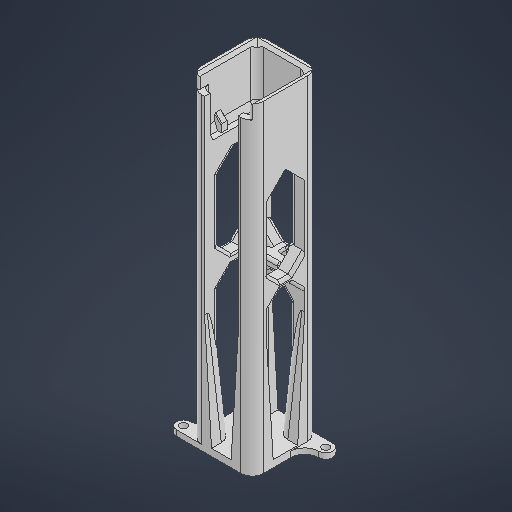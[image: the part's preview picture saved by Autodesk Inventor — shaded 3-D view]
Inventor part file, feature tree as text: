
AUTODESK INVENTOR PART (.ipt)
format: ipt  version: 2025.1 (Build 291241000, 241)  size: 1,649,152 bytes
history: native  units: mm
features: chamfer x13, extrude x10, fillet x10, sketch x7, plane x1, projected_geometry x1
ambient origin geometry x8: Origin, YZ Plane, XZ Plane, XY Plane, X Axis, Y Axis, Z Axis, Center Point
bodies: Solid1 (feature_tree)
feature tree (42):
  sketch  "Sketch1"  dims[d0=39.5mm d1=36.0mm]
  extrude  "Extrusion1"  Depth=36.0mm
  extrude  "Extrusion2"  Depth=47.5mm
  extrude  "Extrusion3"  Depth=6.0mm
  sketch  "Sketch2"  dims[d2=4.0mm d3=47.5mm]
  extrude  "Extrusion4"  Depth=5.0mm
  extrude  "Extrusion5"  Depth=10.0mm TaperAngle=0.0deg
  chamfer  "Chamfer1"  Distance=30.0mm
  chamfer  "Chamfer2"  Distance=180.0mm
  chamfer  "Chamfer4"  Distance=5.0mm
  plane  "Work Plane1"
  chamfer  "Chamfer5"  Distance=5.0mm Angle=45.0deg
  extrude  "Extrusion6"  Depth=4.8mm TaperAngle=45.0deg
  chamfer  "Chamfer6"  Distance=2.0mm Angle=45.0deg
  extrude  "Extrusion7"  Depth=4.8mm TaperAngle=45.0deg
  fillet  "Fillet1"  Radius=70.0mm
  fillet  "Fillet2"  Radius=5.0mm
  fillet  "Fillet3"  Radius=10.0mm
  fillet  "Fillet4"  Radius=10.0mm
  fillet  "Fillet5"  Radius=10.0mm
  extrude  "Extrusion8"  Depth=4.8mm
  sketch  "Sketch6"  dims[d8=10.0mm d9=0.0mm d10=40.0mm d11=0.0mm d12=30.0mm d13=0.0mm]
  extrude  "Extrusion9"  Depth=4.8mm
  chamfer  "Chamfer10"  Distance=10.0mm
  chamfer  "Chamfer11"  Distance=4.0mm
  fillet  "Fillet9"  Radius=10.0mm
  fillet  "Fillet10"  Radius=8.0mm
  chamfer  "Chamfer12"  Distance=1.0mm
  fillet  "Fillet11"  Radius=2.0mm
  fillet  "Fillet12"  Radius=3.0mm
  extrude  "Extrusion11"  Depth=4.8mm TaperAngle=0.0deg
  chamfer  "Chamfer14"  Distance=7.9mm
  chamfer  "Chamfer15"  Distance=10.0mm Angle=45.0deg
  fillet  "Fillet13"  Radius=7.0mm
  chamfer  "Chamfer16"  Distance=2.0mm
  chamfer  "Chamfer17"  Distance=2.0mm
  chamfer  "Chamfer18"  Distance=2.1mm Angle=45.0deg
  sketch  "Sketch4"  dims[d4=44.0mm d5=6.0mm]
  projected_geometry  "Projected Loop1"
  sketch  "Sketch5"  dims[d6=6.0mm d7=5.0mm]
  sketch  "Sketch7"  dims[d14=10.0mm]
  sketch  "Sketch9"  dims[d15=10.0mm d16=180.0mm d17=0.0mm d18=5.0mm d19=0.0mm d20=5.0mm d21=80.0mm d22=45.0deg d23=12.0mm d24=100.0mm d25=45.0deg d29=2.0mm d30=100.0mm d31=45.0deg d32=13.5mm d33=100.0mm d34=45.0deg d35=70.0mm d36=5.0mm d37=0.0mm d38=10.0mm d39=100.0mm d40=45.0deg d41=10.0mm d43=10.0mm d44=5.5mm d46=5.0mm d51=10.0mm d52=10.0mm d53=5.5mm d54=5.0mm d55=4.0mm d56=0.0mm d57=10.0mm d58=8.0mm d59=1.0mm d60=2.0mm d61=3.0mm d62=7.0mm d63=0.0mm d65=7.9mm d66=0.0mm d76=10.0mm d77=7.75mm d78=45.0deg d79=7.0mm d80=7.75mm d81=45.0deg d85=2.0mm d86=2.0mm d87=2.1mm d88=7.75mm d89=45.0deg d90=1.0mm d91=2.0mm d100=4.5mm d101=4.7mm d102=9.4mm d103=10.0mm d104=0.0mm d105=4.5mm d106=2.0mm d107=45.0deg d108=0.6mm d109=2.0mm d110=45.0deg d111=5.0mm d112=2.0mm d113=45.0deg d114=5.0mm d115=2.0mm d116=45.0deg d117=5.0mm d118=2.0mm d119=45.0deg d132=4.8mm]
